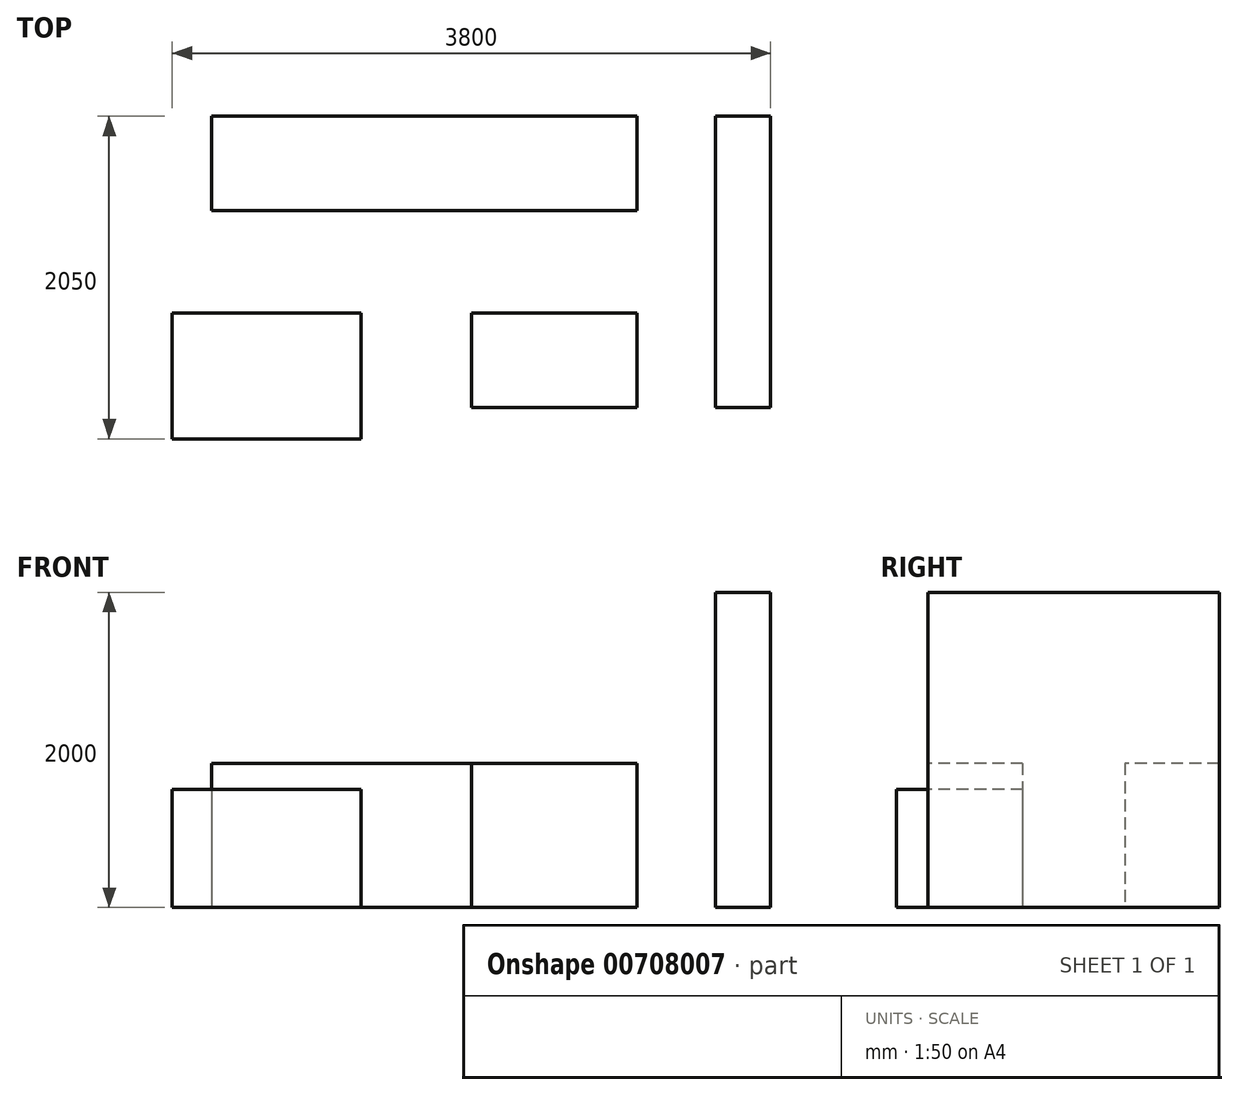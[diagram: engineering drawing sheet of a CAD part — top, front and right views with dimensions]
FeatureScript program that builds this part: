
annotation { "Feature Type Name" : "Feature", "Feature Type Description" : "" }
export const myFeature = defineFeature(function(context is Context, id is Id, definition is map)
    precondition{}
    {
        {
            var Q0;
            Q0=qCreatedBy(makeId("Top.planeOp"),FACE);
            var sketch = newSketch(context, id + "F0", { "sketchPlane" : qUnion([Q0])});
            skLineSegment(sketch, "E0", {"start": v(-4414.87, -2502.5) * mm, "end": v(-4414.87, -1002.5) * mm});
            skLineSegment(sketch, "E1", {"start": v(-4414.87, -1002.5) * mm, "end": v(-4514.87, -1002.5) * mm});
            skLineSegment(sketch, "E2", {"start": v(-4514.87, 547.5) * mm, "end": v(-4414.87, 547.5) * mm});
            skLineSegment(sketch, "E3", {"start": v(-4414.87, 547.5) * mm, "end": v(-4414.87, 697.5) * mm});
            skLineSegment(sketch, "E4", {"start": v(-4414.87, 697.5) * mm, "end": v(-3814.87, 697.5) * mm});
            skLineSegment(sketch, "E5", {"start": v(-3814.87, 697.5) * mm, "end": v(-3814.87, 1297.5) * mm});
            skLineSegment(sketch, "E6", {"start": v(-3814.87, 1297.5) * mm, "end": v(-264.87, 1297.5) * mm});
            skLineSegment(sketch, "E7", {"start": v(-264.87, 1297.5) * mm, "end": v(-264.87, 1197.5) * mm});
            skLineSegment(sketch, "E8", {"start": v(-264.87, 1197.5) * mm, "end": v(-164.87, 1197.5) * mm});
            skLineSegment(sketch, "E9", {"start": v(-164.87, 597.5) * mm, "end": v(-264.87, 597.5) * mm});
            skLineSegment(sketch, "E10", {"start": v(-264.87, 597.5) * mm, "end": v(-264.87, -902.5) * mm});
            skSolve(sketch);
        }
        {
            var Q0;
            Q0 = qSketchRegion(id + "F0", true);
            var Q1;
            Q1 = qConstructionFilter(qBodyType(qCreatedBy(id + "F0" ,EDGE), BodyType.WIRE), ConstructionObject.NO);
            extrude(context, id + "F1", {"entities" : qUnion([Q0]), "bodyType" : ToolBodyType.SURFACE, "surfaceEntities" : qUnion([Q1]), "depth" : 2500 * mm, "offsetDistance" : 25 * mm});
        }
        {
            var Q0;
            Q0=qCreatedBy(makeId("Top.planeOp"),FACE);
            var sketch = newSketch(context, id + "F2", { "sketchPlane" : qUnion([Q0])});
            skLineSegment(sketch, "E11.bottom", {"start": v(-3814.87, 1297.5) * mm, "end": v(-1114.87, 1297.5) * mm});
            skLineSegment(sketch, "E11.top", {"start": v(-3814.87, 697.5) * mm, "end": v(-1114.87, 697.5) * mm});
            skLineSegment(sketch, "E11.left", {"start": v(-3814.87, 1297.5) * mm, "end": v(-3814.87, 697.5) * mm});
            skLineSegment(sketch, "E11.right", {"start": v(-1114.87, 1297.5) * mm, "end": v(-1114.87, 697.5) * mm});
            skLineSegment(sketch, "E12.bottom", {"start": v(-614.87, 1297.5) * mm, "end": v(-264.87, 1297.5) * mm});
            skLineSegment(sketch, "E12.top", {"start": v(-614.87, -552.5) * mm, "end": v(-264.87, -552.5) * mm});
            skLineSegment(sketch, "E12.left", {"start": v(-614.87, 1297.5) * mm, "end": v(-614.87, -552.5) * mm});
            skLineSegment(sketch, "E12.right", {"start": v(-264.87, 1297.5) * mm, "end": v(-264.87, -552.5) * mm});
            skSolve(sketch);
        }
        {
            var Q0;
            Q0=makeQuery(id+"F2.imprint","IMPRINT",FACE,{"disambiguationData":[TD([[makeQuery(id+"F2.imprint","IMPRINT",EDGE,{"derivedFrom":sQuery(id+"F2.wireOp",EDGE,"E11.bottom")}),-1.0]])]});
            extrude(context, id + "F3", {"entities" : qUnion([Q0]), "depth" : 915 * mm, "offsetDistance" : 25 * mm});
        }
        {
            var Q0;
            Q0=makeQuery(id+"F2.imprint","IMPRINT",FACE,{"disambiguationData":[TD([[makeQuery(id+"F2.imprint","IMPRINT",EDGE,{"derivedFrom":sQuery(id+"F2.wireOp",EDGE,"E12.bottom")}),-1.0]])]});
            extrude(context, id + "F4", {"entities" : qUnion([Q0]), "operationType" : NewBodyOperationType.ADD, "depth" : 2000 * mm, "offsetDistance" : 25 * mm});
        }
        {
            var Q0;
            Q0=qCreatedBy(makeId("Top.planeOp"),FACE);
            var sketch = newSketch(context, id + "F5", { "sketchPlane" : qUnion([Q0])});
            skLineSegment(sketch, "E13.bottom", {"start": v(-2164.87, 47.5) * mm, "end": v(-1114.87, 47.5) * mm});
            skLineSegment(sketch, "E13.top", {"start": v(-2164.87, -552.5) * mm, "end": v(-1114.87, -552.5) * mm});
            skLineSegment(sketch, "E13.left", {"start": v(-2164.87, 47.5) * mm, "end": v(-2164.87, -552.5) * mm});
            skLineSegment(sketch, "E13.right", {"start": v(-1114.87, 47.5) * mm, "end": v(-1114.87, -552.5) * mm});
            skLineSegment(sketch, "E14.bottom", {"start": v(-2864.87, 47.5) * mm, "end": v(-4064.87, 47.5) * mm});
            skLineSegment(sketch, "E14.top", {"start": v(-2864.87, -752.5) * mm, "end": v(-4064.87, -752.5) * mm});
            skLineSegment(sketch, "E14.left", {"start": v(-2864.87, 47.5) * mm, "end": v(-2864.87, -752.5) * mm});
            skLineSegment(sketch, "E14.right", {"start": v(-4064.87, 47.5) * mm, "end": v(-4064.87, -752.5) * mm});
            skSolve(sketch);
        }
        {
            var Q0;
            Q0=makeQuery(id+"F5.imprint","IMPRINT",FACE,{"disambiguationData":[TD([[makeQuery(id+"F5.imprint","IMPRINT",EDGE,{"derivedFrom":sQuery(id+"F5.wireOp",EDGE,"E13.bottom")}),-1.0]])]});
            extrude(context, id + "F6", {"entities" : qUnion([Q0]), "depth" : 915 * mm, "offsetDistance" : 25 * mm});
        }
        {
            var Q0;
            Q0=makeQuery(id+"F5.imprint","IMPRINT",FACE,{"disambiguationData":[TD([[makeQuery(id+"F5.imprint","IMPRINT",EDGE,{"derivedFrom":sQuery(id+"F5.wireOp",EDGE,"E14.bottom")}),1.0]])]});
            extrude(context, id + "F7", {"entities" : qUnion([Q0]), "depth" : 750 * mm, "offsetDistance" : 25 * mm});
        }
    });
